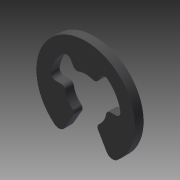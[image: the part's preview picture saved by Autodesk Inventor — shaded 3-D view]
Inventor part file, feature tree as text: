
AUTODESK INVENTOR PART (.ipt)
format: ipt  version: 2014 (Build 180170000, 170)  size: 132,608 bytes
history: native  units: in
note: dims shown in document units (in); Inventor stores cm internally (conversion verified against a paired STEP export)
features: other x7, extrude x1, sketch x1
ambient origin geometry x8: Origin, YZ Plane, XZ Plane, XY Plane, X Axis, Y Axis, Z Axis, Center Point
bodies: Solid1 (feature_tree)
feature tree (9):
  extrude  "Extrusion1"  [1 undecoded]
  other  "RR_XY"
  other  "RR_YZ"
  other  "RR_ZX"
  other  "RR_X"
  other  "RR_Y"
  other  "RR_Z"
  other  "RR_Center"
  sketch  "Sketch_1"  dims[d0=0.0435in d1=0.0in]
note: 1 required parameter value undecoded (feature->parameter linkage not recoverable at this tier; creation-order binding heuristic only, values carry confidence <= 0.55)
